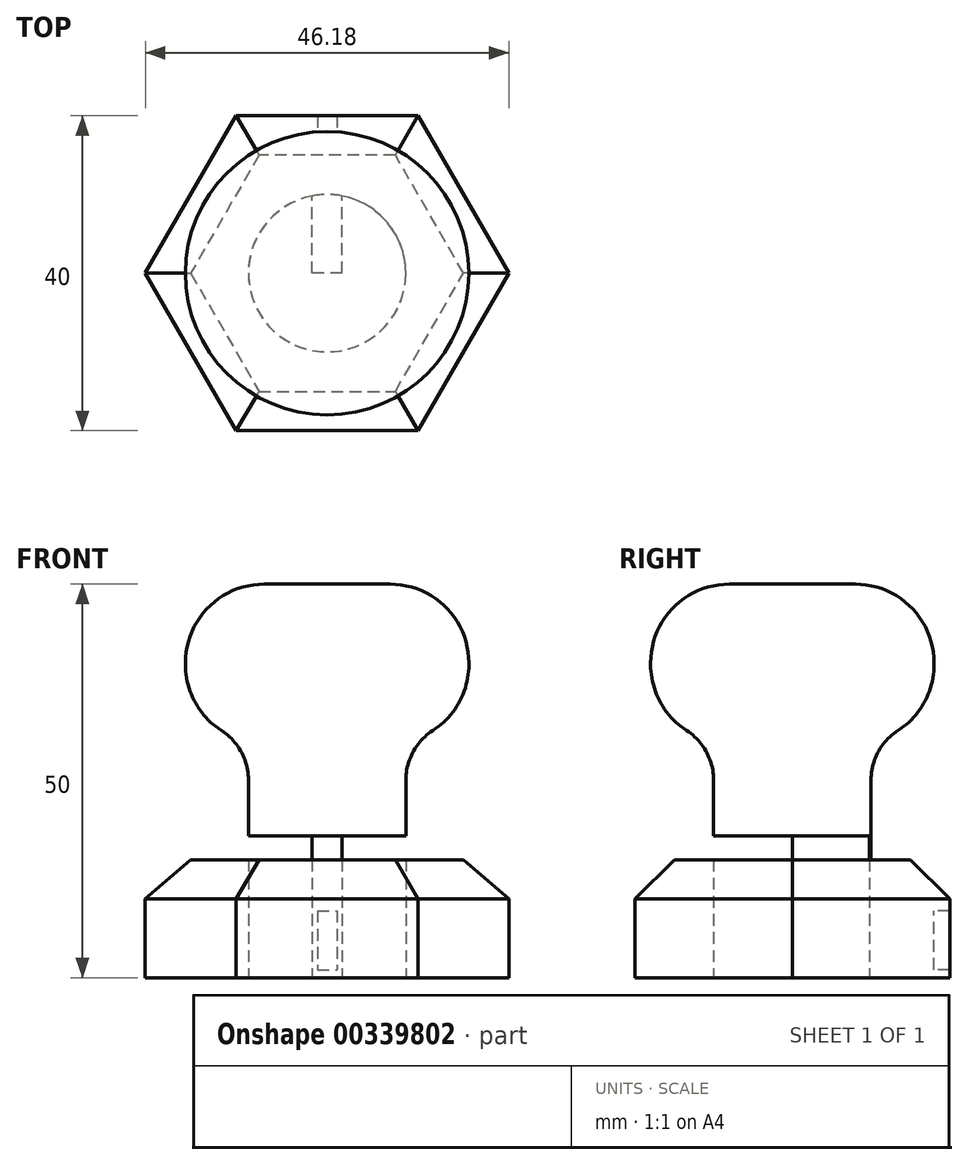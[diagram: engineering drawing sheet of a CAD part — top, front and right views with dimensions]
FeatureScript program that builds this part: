
annotation { "Feature Type Name" : "Feature", "Feature Type Description" : "" }
export const myFeature = defineFeature(function(context is Context, id is Id, definition is map)
    precondition{}
    {
        {
            var Q0;
            Q0=qCreatedBy(makeId("Top.planeOp"),FACE);
            var sketch = newSketch(context, id + "F0", { "sketchPlane" : qUnion([Q0])});
            skCircle(sketch, "E0", {"center": v(0, 0) * mm, "radius": 20 * mm});
            skLineSegment(sketch, "E1", {"start": v(0, 0) * mm, "end": v(25.05, 0) * mm});
            skCircle(sketch, "E2.cCircle", {"center": v(0, 0) * mm, "radius": 20 * mm, "construction": true});
            skLineSegment(sketch, "E2.0", {"start": v(-11.55, 20) * mm, "end": v(11.55, 20) * mm});
            skLineSegment(sketch, "E2.1", {"start": v(11.55, 20) * mm, "end": v(23.1, 0) * mm});
            skLineSegment(sketch, "E2.2", {"start": v(23.1, 0) * mm, "end": v(11.55, -20) * mm});
            skLineSegment(sketch, "E2.3", {"start": v(11.55, -20) * mm, "end": v(-11.55, -20) * mm});
            skLineSegment(sketch, "E2.4", {"start": v(-11.55, -20) * mm, "end": v(-23.1, 0) * mm});
            skLineSegment(sketch, "E2.5", {"start": v(-23.1, 0) * mm, "end": v(-11.55, 20) * mm});
            skPoint(sketch, "E2.0.midPoint", {"position": v(0, 20) * mm});
            skSolve(sketch);
        }
        {
            var Q0;
            Q0 = qSketchRegion(id + "F0", true);
            extrude(context, id + "F1", {"entities" : qUnion([Q0]), "depth" : 15 * mm});
        }
        {
            var Q0;
            Q0=makeQuery(id+"F1.opExtrude","CAP_FACE",FACE,{"disambiguationData":[OSD([sQuery(id+"F0.wireOp",EDGE,"E2.0"),sQuery(id+"F0.wireOp",EDGE,"E2.1"),sQuery(id+"F0.wireOp",EDGE,"E2.2"),sQuery(id+"F0.wireOp",EDGE,"E2.3"),sQuery(id+"F0.wireOp",EDGE,"E2.4"),sQuery(id+"F0.wireOp",EDGE,"E2.5")])],"isStart":false});
            var sketch = newSketch(context, id + "F2", { "sketchPlane" : qUnion([Q0])});
            skCircle(sketch, "E3", {"center": v(0, 0) * mm, "radius": 10 * mm});
            skSolve(sketch);
        }
        {
            var Q0;
            Q0 = qSketchRegion(id + "F2", true);
            extrude(context, id + "F3", {"entities" : qUnion([Q0]), "operationType" : NewBodyOperationType.ADD, "depth" : 15 * mm});
        }
        {
            var Q0;
            Q0=makeQuery(id+"F3.opExtrude","CAP_FACE",FACE,{"disambiguationData":[OSD([sQuery(id+"F2.wireOp",EDGE,"E3")])],"isStart":false});
            var sketch = newSketch(context, id + "F4", { "sketchPlane" : qUnion([Q0])});
            skCircle(sketch, "E4", {"center": v(0, 0) * mm, "radius": 18 * mm});
            skSolve(sketch);
        }
        {
            var Q0;
            Q0 = qSketchRegion(id + "F4", true);
            extrude(context, id + "F5", {"entities" : qUnion([Q0]), "operationType" : NewBodyOperationType.ADD, "depth" : 20 * mm});
        }
        {
            var Q0;
            Q0=makeQuery(id+"F5.opExtrude","CAP_EDGE",EDGE,{"disambiguationData":[OSD([sQuery(id+"F4.wireOp",EDGE,"E4")])],"isStart":true});
            var Q1;
            Q1=makeQuery(id+"F5.opExtrude","CAP_EDGE",EDGE,{"disambiguationData":[OSD([sQuery(id+"F4.wireOp",EDGE,"E4")])],"isStart":false});
            fillet(context, id + "F6", {"entities" : qUnion([Q0, Q1]), "radius" : 10 * mm, "tangentPropagation" : true, "allowEdgeOverflow" : false});
        }
        {
            var Q0;
            Q0=makeQuery(id+"F6.opFillet","BLEND_EDGE",EDGE,{"blendedFrom":[makeQuery(id+"F5.opExtrude","CAP_EDGE",EDGE,{"disambiguationData":[OSD([sQuery(id+"F4.wireOp",EDGE,"E4")])],"isStart":true}),makeQuery(id+"F3.opExtrude","SWEPT_FACE",FACE,{"disambiguationData":[OSD([sQuery(id+"F2.wireOp",EDGE,"E3")])]})],"blendedInto":[makeQuery(id+"F3.opExtrude","SWEPT_FACE",FACE,{"disambiguationData":[OSD([sQuery(id+"F2.wireOp",EDGE,"E3")])]})]});
            var Q1;
            Q1=makeQuery(id+"F3.opExtrude","CAP_EDGE",EDGE,{"disambiguationData":[OSD([sQuery(id+"F2.wireOp",EDGE,"E3")])],"isStart":true});
            fillet(context, id + "F7", {"entities" : qUnion([Q0, Q1]), "radius" : 7.5 * mm, "tangentPropagation" : true, "allowEdgeOverflow" : false});
        }
        {
            var Q0;
            Q0=qCreatedBy(makeId("Front.planeOp"),FACE);
            var sketch = newSketch(context, id + "F8", { "sketchPlane" : qUnion([Q0])});
            skLineSegment(sketch, "E5", {"start": v(0, 0) * mm, "end": v(0, 1) * mm});
            skLineSegment(sketch, "E6.bottom", {"start": v(0, 1) * mm, "end": v(-1.25, 1) * mm});
            skLineSegment(sketch, "E6.top", {"start": v(0, 8.5) * mm, "end": v(-1.25, 8.5) * mm});
            skLineSegment(sketch, "E6.left", {"start": v(0, 1) * mm, "end": v(0, 8.5) * mm});
            skLineSegment(sketch, "E6.right", {"start": v(-1.25, 1) * mm, "end": v(-1.25, 8.5) * mm});
            skPoint(sketch, "E7.oppositeSnap0", {"position": v(-0.63, 8.5) * mm});
            skLineSegment(sketch, "E7.bottom", {"start": v(0, 1) * mm, "end": v(1.25, 1) * mm});
            skLineSegment(sketch, "E7.top", {"start": v(0, 8.5) * mm, "end": v(1.25, 8.5) * mm});
            skLineSegment(sketch, "E7.right", {"start": v(1.25, 1) * mm, "end": v(1.25, 8.5) * mm});
            skSolve(sketch);
        }
        {
            var Q0;
            Q0 = qSketchRegion(id + "F8", true);
            extrude(context, id + "F9", {"entities" : qUnion([Q0]), "operationType" : NewBodyOperationType.REMOVE, "oppositeDirection" : true, "depth" : 25 * mm, "hasSecondDirection" : true, "secondDirectionOppositeDirection" : true, "secondDirectionDepth" : 18 * mm});
        }
        {
            var Q0;
            Q0=makeQuery(id+"F1.opExtrude","CAP_FACE",FACE,{"disambiguationData":[OSD([sQuery(id+"F0.wireOp",EDGE,"E2.0"),sQuery(id+"F0.wireOp",EDGE,"E2.1"),sQuery(id+"F0.wireOp",EDGE,"E2.2"),sQuery(id+"F0.wireOp",EDGE,"E2.3"),sQuery(id+"F0.wireOp",EDGE,"E2.4"),sQuery(id+"F0.wireOp",EDGE,"E2.5")])],"isStart":true});
            var sketch = newSketch(context, id + "F10", { "sketchPlane" : qUnion([Q0])});
            skCircle(sketch, "E8", {"center": v(0, 0) * mm, "radius": 10 * mm});
            skLineSegment(sketch, "E9", {"start": v(0, 0) * mm, "end": v(0, 2) * mm});
            skLineSegment(sketch, "E10", {"start": v(0, 2) * mm, "end": v(9.8, 2) * mm});
            skLineSegment(sketch, "E11", {"start": v(9.8, 2) * mm, "end": v(0, 2) * mm});
            skLineSegment(sketch, "E12", {"start": v(0, 0) * mm, "end": v(0, -2) * mm});
            skLineSegment(sketch, "E13", {"start": v(0, -2) * mm, "end": v(9.8, -2) * mm});
            skLineSegment(sketch, "E14", {"start": v(0, 0) * mm, "end": v(1.9, 0) * mm});
            skLineSegment(sketch, "E15", {"start": v(1.9, 0) * mm, "end": v(1.9, -9.82) * mm});
            skLineSegment(sketch, "E16", {"start": v(0, 0) * mm, "end": v(-1.9, 0) * mm});
            skLineSegment(sketch, "E17", {"start": v(-1.9, 0) * mm, "end": v(-1.9, -9.82) * mm});
            skSolve(sketch);
        }
        {
            var Q0;
            Q0=makeQuery(id+"F10.imprint","IMPRINT",FACE,{"disambiguationData":[TD([[makeQuery(id+"F10.imprint","IMPRINT",EDGE,{"derivedFrom":sQuery(id+"F10.wireOp",EDGE,"E9")}),1.0]])]});
            var Q1;
            Q1=makeQuery(id+"F10.imprint","IMPRINT",FACE,{"disambiguationData":[TD([[makeQuery(id+"F10.imprint","IMPRINT",EDGE,{"derivedFrom":sQuery(id+"F10.wireOp",EDGE,"E9")}),-1.0]])]});
            var Q2;
            {var subQ0=sQuery(id+"F10.wireOp",EDGE,"E13");var subQ1=sQuery(id+"F10.wireOp",EDGE,"E8");var subQ2=makeQuery(id+"F10.imprint","INTERSECT",VERTEX,{"derivedFrom":[subQ1,subQ0]});Q2=makeQuery(id+"F10.imprint","IMPRINT",FACE,{"disambiguationData":[TD([[makeQuery(id+"F10.imprint","IMPRINT",EDGE,{"disambiguationData":[TD([[subQ2,1.0]])],"derivedFrom":subQ1}),1.0]])]});}
            extrude(context, id + "F11", {"entities" : qUnion([Q0, Q1, Q2]), "operationType" : NewBodyOperationType.REMOVE, "oppositeDirection" : true, "depth" : 18 * mm});
        }
        {
            var Q0;
            Q0=makeQuery(id+"F1.opExtrude","CAP_EDGE",EDGE,{"disambiguationData":[OSD([sQuery(id+"F0.wireOp",EDGE,"E2.4")])],"isStart":false});
            var Q1;
            Q1=makeQuery(id+"F1.opExtrude","CAP_EDGE",EDGE,{"disambiguationData":[OSD([sQuery(id+"F0.wireOp",EDGE,"E2.5")])],"isStart":false});
            var Q2;
            Q2=makeQuery(id+"F1.opExtrude","CAP_EDGE",EDGE,{"disambiguationData":[OSD([sQuery(id+"F0.wireOp",EDGE,"E2.0")])],"isStart":false});
            var Q3;
            Q3=makeQuery(id+"F1.opExtrude","CAP_EDGE",EDGE,{"disambiguationData":[OSD([sQuery(id+"F0.wireOp",EDGE,"E2.1")])],"isStart":false});
            var Q4;
            Q4=makeQuery(id+"F1.opExtrude","CAP_EDGE",EDGE,{"disambiguationData":[OSD([sQuery(id+"F0.wireOp",EDGE,"E2.3")])],"isStart":false});
            var Q5;
            Q5=makeQuery(id+"F1.opExtrude","CAP_EDGE",EDGE,{"disambiguationData":[OSD([sQuery(id+"F0.wireOp",EDGE,"E2.2")])],"isStart":false});
            chamfer(context, id + "F12", {"entities" : qUnion([Q0, Q1, Q2, Q3, Q4, Q5]), "width" : 5 * mm, "tangentPropagation" : true});
        }
    });
